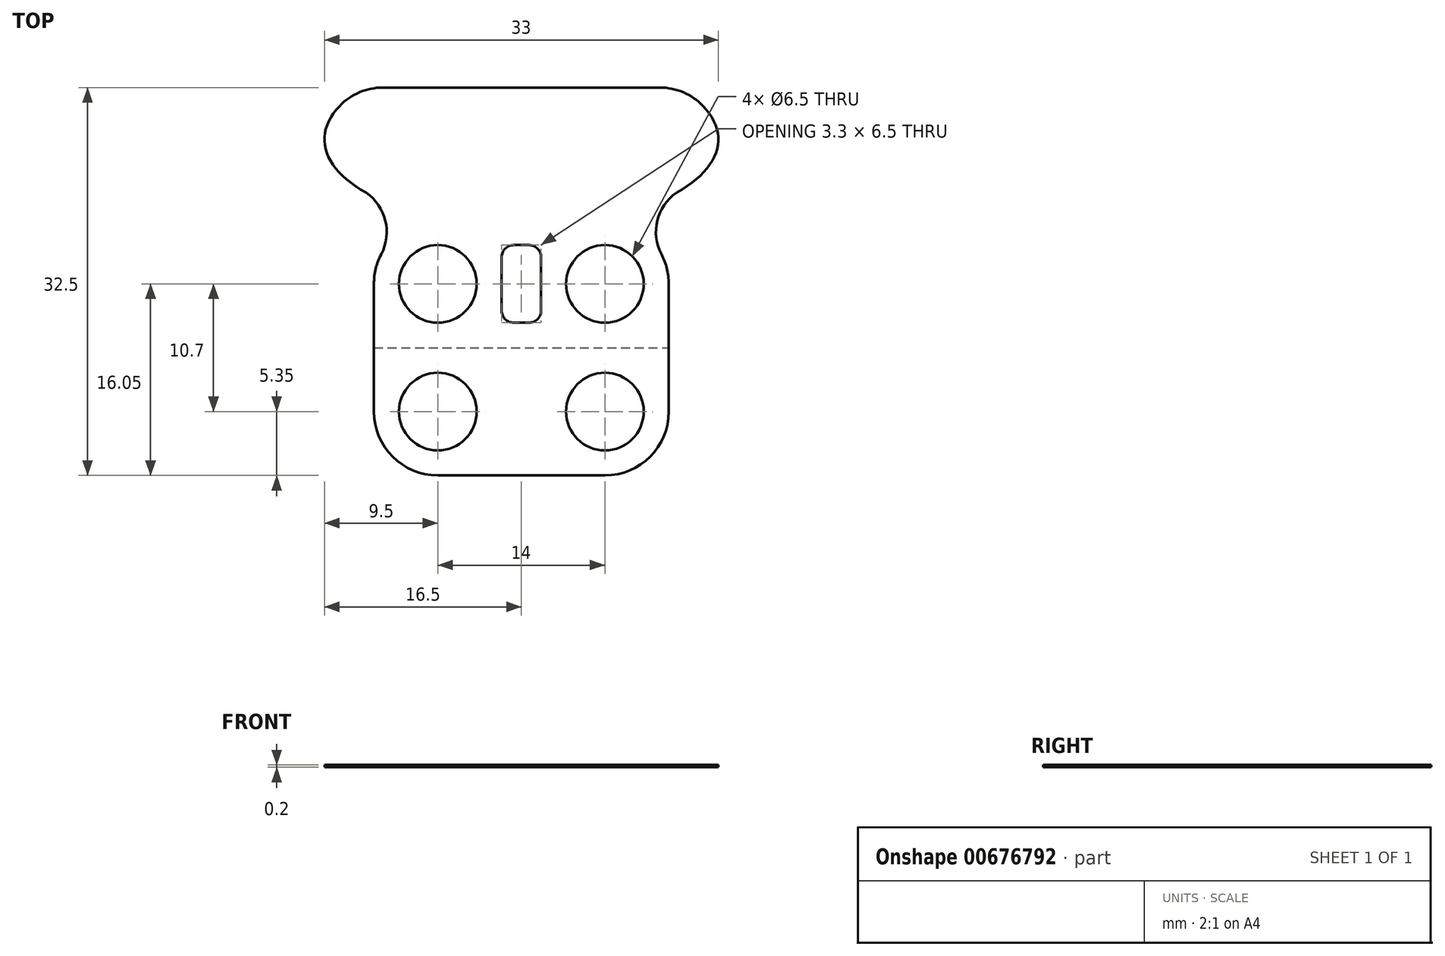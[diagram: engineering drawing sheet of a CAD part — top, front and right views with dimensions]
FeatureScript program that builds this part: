
annotation { "Feature Type Name" : "Feature", "Feature Type Description" : "" }
export const myFeature = defineFeature(function(context is Context, id is Id, definition is map)
    precondition{}
    {
        {
            var Q0;
            Q0=qCreatedBy(makeId("Top.planeOp"),FACE);
            var sketch = newSketch(context, id + "F0", { "sketchPlane" : qUnion([Q0])});
            skLineSegment(sketch, "E0", {"start": v(-13.2, 4.35) * mm, "end": v(13.2, 4.35) * mm});
            skPoint(sketch, "E1", {"position": v(0, -7.25) * mm});
            skCircle(sketch, "E2", {"center": v(-7, -12.1) * mm, "radius": 3.25 * mm});
            skLineSegment(sketch, "E3", {"start": v(0, 24.36) * mm, "end": v(0, -25.37) * mm, "construction": true});
            skPoint(sketch, "E4", {"position": v(-7, -17.45) * mm});
            skEllipticalArc(sketch, "E5", {});
            skEllipticalArc(sketch, "E6", {"construction": true});
            skEllipticalArc(sketch, "E7", {"construction": true});
            skEllipticalArc(sketch, "E8", {"construction": true});
            skArc(sketch, "E9", {"start": v(-11.74, -9.61) * mm, "mid": v(-12.2, -10.82) * mm, "end": v(-12.35, -12.1) * mm});
            skArc(sketch, "E10", {"start": v(-3.96, -7.7) * mm, "mid": v(-8.28, -6.9) * mm, "end": v(-11.74, -9.61) * mm, "construction": true});
            skCircle(sketch, "E11.MirrorC", {"center": v(7, -12.1) * mm, "radius": 3.25 * mm});
            skArc(sketch, "E12.MirrorCS", {"start": v(11.74, -9.61) * mm, "mid": v(12.2, -10.82) * mm, "end": v(12.35, -12.1) * mm});
            skEllipticalArc(sketch, "E13", {"construction": true});
            skEllipticalArc(sketch, "E14", {});
            skLineSegment(sketch, "E15", {"start": v(-7, -17.45) * mm, "end": v(7, -17.45) * mm, "construction": true});
            skCircle(sketch, "E16.MirrorC", {"center": v(7, -22.8) * mm, "radius": 3.25 * mm});
            skCircle(sketch, "E17.MirrorC", {"center": v(-7, -22.8) * mm, "radius": 3.25 * mm});
            skPoint(sketch, "E18", {"position": v(-7, -28.15) * mm});
            skLineSegment(sketch, "E19", {"start": v(-7, -28.15) * mm, "end": v(7, -28.15) * mm});
            skArc(sketch, "E20", {"start": v(-12.35, -12.1) * mm, "mid": v(-9.6, -16.77) * mm, "end": v(-4.19, -16.65) * mm, "construction": true});
            skArc(sketch, "E21", {"start": v(-4.19, -16.65) * mm, "mid": v(-1.65, -12.23) * mm, "end": v(-3.96, -7.7) * mm, "construction": true});
            skArc(sketch, "E22", {"start": v(-12.35, -22.8) * mm, "mid": v(-10.78, -26.58) * mm, "end": v(-7, -28.15) * mm});
            skArc(sketch, "E23", {"start": v(-7, -28.15) * mm, "mid": v(-3.22, -19.02) * mm, "end": v(-12.35, -22.8) * mm, "construction": true});
            skArc(sketch, "E24", {"start": v(12.35, -22.8) * mm, "mid": v(3.22, -19.02) * mm, "end": v(7, -28.15) * mm, "construction": true});
            skArc(sketch, "E25", {"start": v(7, -28.15) * mm, "mid": v(10.78, -26.58) * mm, "end": v(12.35, -22.8) * mm});
            skArc(sketch, "E26", {"start": v(12.35, -12.1) * mm, "mid": v(9.6, -16.77) * mm, "end": v(4.19, -16.65) * mm, "construction": true});
            skArc(sketch, "E27", {"start": v(4.19, -16.65) * mm, "mid": v(1.65, -12.23) * mm, "end": v(3.96, -7.7) * mm, "construction": true});
            skLineSegment(sketch, "E28", {"start": v(12.35, -12.1) * mm, "end": v(12.35, -22.8) * mm});
            skLineSegment(sketch, "E29", {"start": v(-12.35, -12.1) * mm, "end": v(-12.35, -22.8) * mm});
            skArc(sketch, "E30", {"start": v(-11.74, -9.61) * mm, "mid": v(-11.4, -6.8) * mm, "end": v(-13, -4.46) * mm});
            skArc(sketch, "E31", {"start": v(13, -4.46) * mm, "mid": v(11.4, -6.8) * mm, "end": v(11.74, -9.61) * mm});
            skLineSegment(sketch, "E32.bottom", {"start": v(-1.65, -8.85) * mm, "end": v(1.65, -8.85) * mm});
            skLineSegment(sketch, "E32.top", {"start": v(-1.65, -15.35) * mm, "end": v(1.65, -15.35) * mm});
            skLineSegment(sketch, "E32.left", {"start": v(-1.65, -8.85) * mm, "end": v(-1.65, -15.35) * mm});
            skLineSegment(sketch, "E32.right", {"start": v(1.65, -8.85) * mm, "end": v(1.65, -15.35) * mm});
            const initialGuessF0  = {"E5": [0, 0, 1, 0, 0.0165, 0.00725, 2.49809154479651, 3.805032087827234], "E6": [0, 0, 1, 0, 0.0165, 0.00725, 0.6435011087932834, 2.49809154479651], "E7": [0, 0, 1, 0, 0.0165, 0.00725, 3.805032087827234, 4.484235995839755], "E8": [0, 0, 1, 0, 0.0165, 0.00725, 4.484235995839755, 4.940541964929625], "E13": [0, 0, 1, 0, 0.0165, 0.00725, 4.940541964929625, 5.619745872942145], "E14": [0, 0, 1, 0, 0.0165, 0.00725, 5.619745872942145, 0.6435011087932834]};
            skSetInitialGuess(sketch, initialGuessF0);
            skSolve(sketch);
        }
        {
            var Q0;
            Q0=makeQuery(id+"F0.imprint","IMPRINT",FACE,{"disambiguationData":[TD([[makeQuery(id+"F0.imprint","IMPRINT",EDGE,{"derivedFrom":sQuery(id+"F0.wireOp",EDGE,"E0")}),-1.0]])]});
            extrude(context, id + "F1", {"entities" : qUnion([Q0]), "depth" : 0.2 * mm, "offsetDistance" : 25 * mm});
        }
        {
            var Q0;
            Q0=makeQuery(id+"F1.opExtrude","SWEPT_EDGE",EDGE,{"disambiguationData":[OSD([sQuery(id+"F0.wireOp",EDGE,"E0"),sQuery(id+"F0.wireOp",EDGE,"E14")])]});
            var Q1;
            Q1=makeQuery(id+"F1.opExtrude","SWEPT_EDGE",EDGE,{"disambiguationData":[OSD([sQuery(id+"F0.wireOp",EDGE,"E0"),sQuery(id+"F0.wireOp",EDGE,"E5")])]});
            fillet(context, id + "F2", {"entities" : qUnion([Q0, Q1]), "radius" : 5 * mm, "tangentPropagation" : true, "allowEdgeOverflow" : false});
        }
        {
            var Q0;
            Q0=makeQuery(id+"F1.opExtrude","CAP_FACE",FACE,{"disambiguationData":[OSD([sQuery(id+"F0.wireOp",EDGE,"E0"),sQuery(id+"F0.wireOp",EDGE,"E2"),sQuery(id+"F0.wireOp",EDGE,"CHCftW8w-065h-tQDZ-IhoU-abju6eTLG0Pv"),sQuery(id+"F0.wireOp",EDGE,"KbDhvPpw-rd1N-rmwO-lzf3-fwdg6Sh6NQGA"),sQuery(id+"F0.wireOp",EDGE,"E5"),sQuery(id+"F0.wireOp",EDGE,"E8"),sQuery(id+"F0.wireOp",EDGE,"E9"),sQuery(id+"F0.wireOp",EDGE,"d9a823b4-093e-4013-9511-6d8e921653f30.MirrorCS"),sQuery(id+"F0.wireOp",EDGE,"E11.MirrorC"),sQuery(id+"F0.wireOp",EDGE,"E12.MirrorCS"),sQuery(id+"F0.wireOp",EDGE,"d9a823b4-093e-4013-9511-6d8e921653f33.MirrorCS"),sQuery(id+"F0.wireOp",EDGE,"E14"),sQuery(id+"F0.wireOp",EDGE,"E16.MirrorC"),sQuery(id+"F0.wireOp",EDGE,"E17.MirrorC"),sQuery(id+"F0.wireOp",EDGE,"E19"),sQuery(id+"F0.wireOp",EDGE,"QmyDyBqd-bj7z-RgfA-sde7-up26nTUJPYr9"),sQuery(id+"F0.wireOp",EDGE,"YLmbDcTL-PodD-xdQN-eUku-qUKalcZCoei6"),sQuery(id+"F0.wireOp",EDGE,"2ec8a928-fbb5-42e5-82c7-20d656f9ea090.MirrorCS"),sQuery(id+"F0.wireOp",EDGE,"E21"),sQuery(id+"F0.wireOp",EDGE,"E22"),sQuery(id+"F0.wireOp",EDGE,"E25"),sQuery(id+"F0.wireOp",EDGE,"E27")])],"isStart":true});
            var sketch = newSketch(context, id + "F3", { "sketchPlane" : qUnion([Q0])});
            skLineSegment(sketch, "E33", {"start": v(-12.35, 17.45) * mm, "end": v(12.35, 17.45) * mm, "construction": true});
            skLineSegment(sketch, "E34.bottom", {"start": v(-12.35, 17.46) * mm, "end": v(12.35, 17.46) * mm});
            skLineSegment(sketch, "E34.top", {"start": v(-12.35, 17.44) * mm, "end": v(12.35, 17.44) * mm});
            skLineSegment(sketch, "E34.left", {"start": v(-12.35, 17.46) * mm, "end": v(-12.35, 17.44) * mm});
            skLineSegment(sketch, "E34.right", {"start": v(12.35, 17.46) * mm, "end": v(12.35, 17.44) * mm});
            skSolve(sketch);
        }
        {
            var Q0;
            Q0=qSketchRegion(id+"F3",true);
            extrude(context, id + "F4", {"entities" : qUnion([Q0]), "operationType" : NewBodyOperationType.REMOVE, "oppositeDirection" : true, "depth" : 0.02 * mm, "offsetDistance" : 25 * mm});
        }
        {
            var Q0;
            Q0=makeQuery(id+"F1.opExtrude","SWEPT_EDGE",EDGE,{"disambiguationData":[OSD([sQuery(id+"F0.wireOp",EDGE,"E32.bottom"),sQuery(id+"F0.wireOp",EDGE,"E32.left")])]});
            var Q1;
            Q1=makeQuery(id+"F1.opExtrude","SWEPT_EDGE",EDGE,{"disambiguationData":[OSD([sQuery(id+"F0.wireOp",EDGE,"E32.bottom"),sQuery(id+"F0.wireOp",EDGE,"E32.right")])]});
            var Q2;
            Q2=makeQuery(id+"F1.opExtrude","SWEPT_EDGE",EDGE,{"disambiguationData":[OSD([sQuery(id+"F0.wireOp",EDGE,"E32.top"),sQuery(id+"F0.wireOp",EDGE,"E32.left")])]});
            var Q3;
            Q3=makeQuery(id+"F1.opExtrude","SWEPT_EDGE",EDGE,{"disambiguationData":[OSD([sQuery(id+"F0.wireOp",EDGE,"E32.top"),sQuery(id+"F0.wireOp",EDGE,"E32.right")])]});
            fillet(context, id + "F5", {"entities" : qUnion([Q0, Q1, Q2, Q3]), "radius" : 1 * mm, "tangentPropagation" : true, "allowEdgeOverflow" : false});
        }
    });
